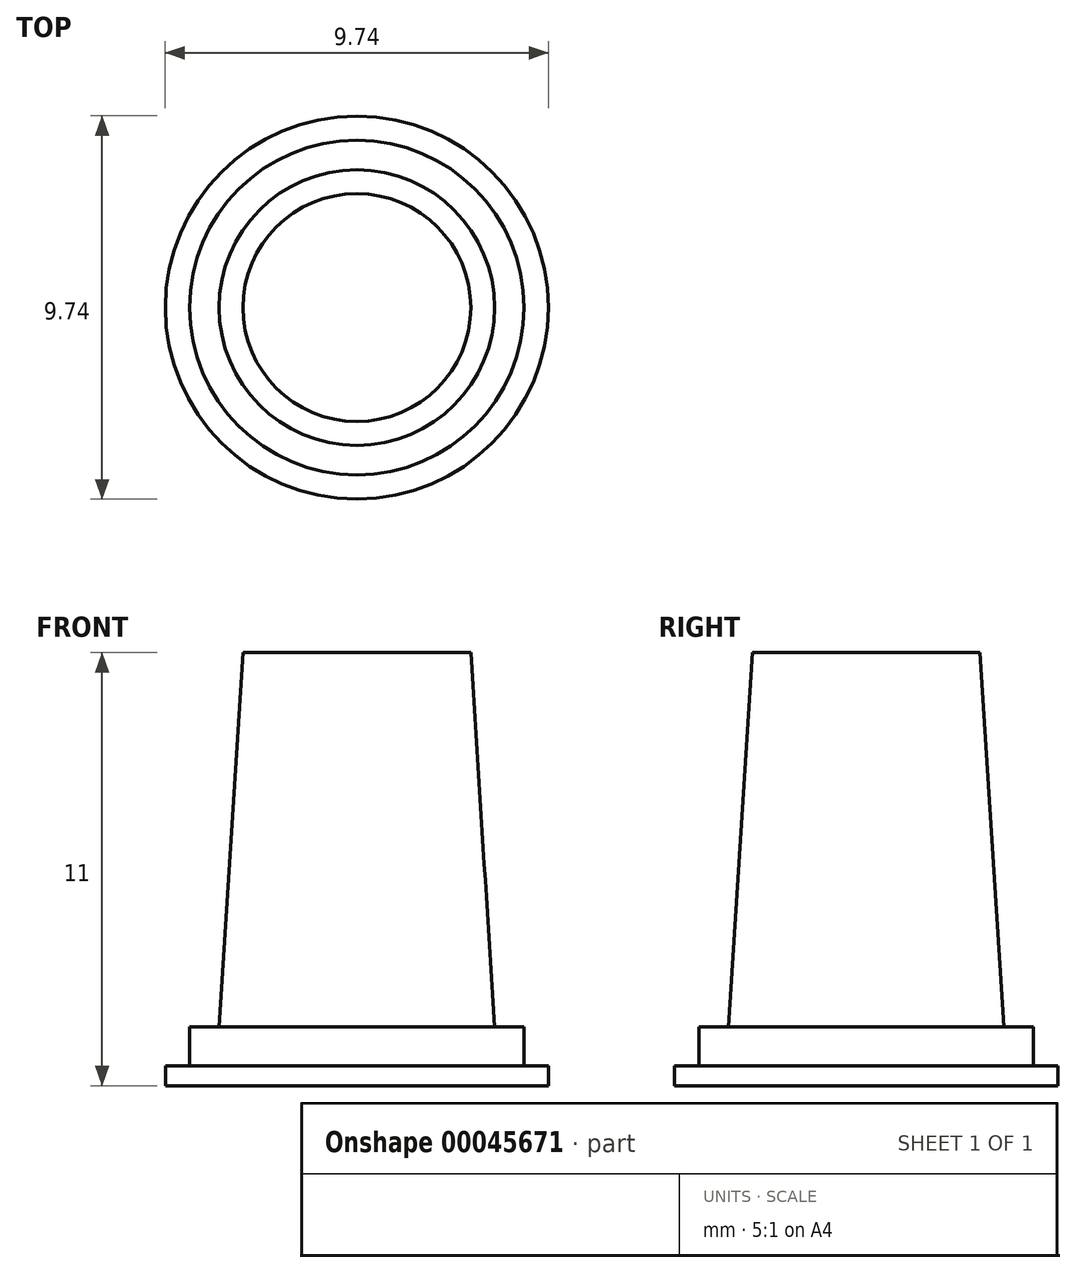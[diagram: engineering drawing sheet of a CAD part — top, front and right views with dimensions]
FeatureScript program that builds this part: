
annotation { "Feature Type Name" : "Feature", "Feature Type Description" : "" }
export const myFeature = defineFeature(function(context is Context, id is Id, definition is map)
    precondition{}
    {
        {
            var Q0;
            Q0=qCreatedBy(makeId("Top.planeOp"),FACE);
            var sketch = newSketch(context, id + "F0", { "sketchPlane" : qUnion([Q0])});
            skCircle(sketch, "E0", {"center": v(0, 0) * mm, "radius": 3.5 * mm});
            skSolve(sketch);
        }
        {
            var Q0;
            Q0=makeQuery(id+"F0.imprint","IMPRINT",FACE,{"disambiguationData":[TD([[makeQuery(id+"F0.imprint","IMPRINT",EDGE,{"derivedFrom":sQuery(id+"F0.wireOp",EDGE,"E0")}),1.0]])]});
            cPlane(context, id + "F1", {"entities" : qUnion([Q0]), "cplaneType" : CPlaneType.OFFSET, "offset" : 9.5 * mm, "width" : 150 * mm, "height" : 150 * mm});
        }
        {
            var Q0;
            Q0=qCreatedBy(id+"F1.planeOp",FACE);
            var sketch = newSketch(context, id + "F2", { "sketchPlane" : qUnion([Q0])});
            skCircle(sketch, "E1", {"center": v(0, 0) * mm, "radius": 2.9 * mm});
            skSolve(sketch);
        }
        {
            var Q0;
            Q0 = qSketchRegion(id + "F0", true);
            var Q1;
            Q1 = qSketchRegion(id + "F2", true);
            loft(context, id + "F3", {"sheetProfilesArray" : [{ "sheetProfileEntities" : qUnion([Q0]) }, { "sheetProfileEntities" : qUnion([Q1]) }]});
        }
        {
            var Q0;
            Q0=makeQuery(id+"F3.opLoft","CAP_FACE",FACE,{"disambiguationData":[OSD([makeQuery(id+"F0.imprint","IMPRINT",FACE,{"disambiguationData":[TD([[makeQuery(id+"F0.imprint","IMPRINT",EDGE,{"derivedFrom":sQuery(id+"F0.wireOp",EDGE,"E0")}),1.0]])]})])],"isStart":true});
            var sketch = newSketch(context, id + "F4", { "sketchPlane" : qUnion([Q0])});
            skCircle(sketch, "E2", {"center": v(0, 0) * mm, "radius": 4.25 * mm});
            skSolve(sketch);
        }
        {
            var Q0;
            Q0 = qSketchRegion(id + "F4", true);
            extrude(context, id + "F5", {"entities" : qUnion([Q0]), "operationType" : NewBodyOperationType.ADD, "depth" : 1 * mm});
        }
        {
            var Q0;
            Q0=makeQuery(id+"F5.opExtrude","CAP_FACE",FACE,{"disambiguationData":[OSD([sQuery(id+"F4.wireOp",EDGE,"E2")])],"isStart":false});
            var sketch = newSketch(context, id + "F6", { "sketchPlane" : qUnion([Q0])});
            skCircle(sketch, "E3", {"center": v(0, 0) * mm, "radius": 4.87 * mm});
            skSolve(sketch);
        }
        {
            var Q0;
            Q0 = qSketchRegion(id + "F6", true);
            extrude(context, id + "F7", {"entities" : qUnion([Q0]), "operationType" : NewBodyOperationType.ADD, "depth" : .5 * mm});
        }
    });
